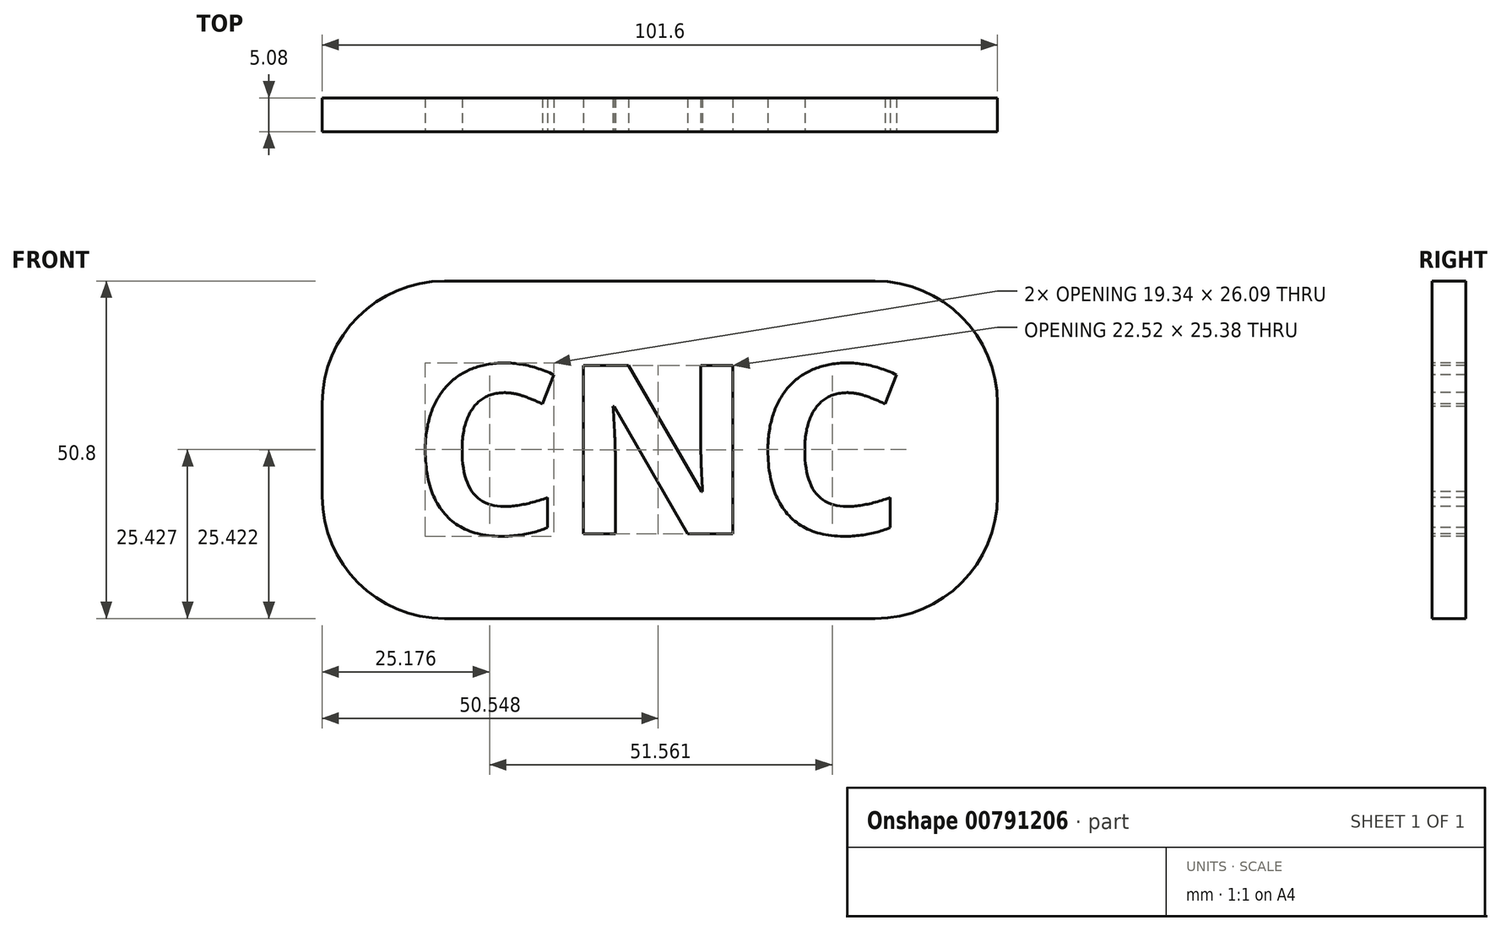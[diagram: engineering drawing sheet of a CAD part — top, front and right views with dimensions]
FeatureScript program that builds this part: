
annotation { "Feature Type Name" : "Feature", "Feature Type Description" : "" }
export const myFeature = defineFeature(function(context is Context, id is Id, definition is map)
    precondition{}
    {
        {
            var Q0;
            Q0=qCreatedBy(makeId("Front.planeOp"),FACE);
            var sketch = newSketch(context, id + "F0", { "sketchPlane" : qUnion([Q0])});
            skLineSegment(sketch, "E0.bottom", {"start": v(50.8, -25.4) * mm, "end": v(-50.8, -25.4) * mm});
            skLineSegment(sketch, "E0.top", {"start": v(50.8, 25.4) * mm, "end": v(-50.8, 25.4) * mm});
            skLineSegment(sketch, "E0.left", {"start": v(50.8, -25.4) * mm, "end": v(50.8, 25.4) * mm});
            skLineSegment(sketch, "E0.right", {"start": v(-50.8, -25.4) * mm, "end": v(-50.8, 25.4) * mm});
            skPoint(sketch, "E0.middle", {"position": v(0, 0) * mm});
            skSolve(sketch);
        }
        {
            var Q0;
            Q0=qSketchRegion(id+"F0",true);
            extrude(context, id + "F1", {"entities" : qUnion([Q0]), "depth" : 5.08 * mm});
        }
        {
            var Q0;
            Q0=makeQuery(id+"F1.opExtrude","SWEPT_EDGE",EDGE,{"disambiguationData":[OSD([sQuery(id+"F0.wireOp",EDGE,"E0.top"),sQuery(id+"F0.wireOp",EDGE,"E0.right")])]});
            var Q1;
            Q1=makeQuery(id+"F1.opExtrude","SWEPT_EDGE",EDGE,{"disambiguationData":[OSD([sQuery(id+"F0.wireOp",EDGE,"E0.top"),sQuery(id+"F0.wireOp",EDGE,"E0.left")])]});
            var Q2;
            Q2=makeQuery(id+"F1.opExtrude","SWEPT_EDGE",EDGE,{"disambiguationData":[OSD([sQuery(id+"F0.wireOp",EDGE,"E0.bottom"),sQuery(id+"F0.wireOp",EDGE,"E0.left")])]});
            var Q3;
            Q3=makeQuery(id+"F1.opExtrude","SWEPT_EDGE",EDGE,{"disambiguationData":[OSD([sQuery(id+"F0.wireOp",EDGE,"E0.bottom"),sQuery(id+"F0.wireOp",EDGE,"E0.right")])]});
            fillet(context, id + "F2", {"entities" : qUnion([Q0, Q1, Q2, Q3]), "radius" : 18.4 * mm, "tangentPropagation" : true, "allowEdgeOverflow" : false});
        }
        {
            var Q0;
            Q0=makeQuery(id+"F1.opExtrude","CAP_FACE",FACE,{"disambiguationData":[OSD([sQuery(id+"F0.wireOp",EDGE,"E0.bottom"),sQuery(id+"F0.wireOp",EDGE,"E0.top"),sQuery(id+"F0.wireOp",EDGE,"E0.left"),sQuery(id+"F0.wireOp",EDGE,"E0.right")])],"isStart":false});
            var sketch = newSketch(context, id + "F3", { "sketchPlane" : qUnion([Q0])});
            skText(sketch, "E1", { "text": "CNC", "fontName": "OpenSans-Bold.ttf"});
            const initialGuessF3  = {"E1": [-0.03736, -0.01267, 1, 0, 0.0256]};
            skSetInitialGuess(sketch, initialGuessF3);
            skSolve(sketch);
        }
        {
            var Q0;
            Q0 = qSketchRegion(id + "F3", true);
            var Q1;
            Q1=makeQuery(id+"F1.opExtrude","CAP_FACE",FACE,{"disambiguationData":[OSD([sQuery(id+"F0.wireOp",EDGE,"E0.bottom"),sQuery(id+"F0.wireOp",EDGE,"E0.top"),sQuery(id+"F0.wireOp",EDGE,"E0.left"),sQuery(id+"F0.wireOp",EDGE,"E0.right")])],"isStart":true});
            extrude(context, id + "F4", {"entities" : qUnion([Q0]), "operationType" : NewBodyOperationType.REMOVE, "endBound" : BoundingType.UP_TO_SURFACE, "oppositeDirection" : true, "depth" : 25.4 * mm, "endBoundEntityFace" : qUnion([Q1]), "offsetDistance" : 25.4 * mm});
        }
    });
